# Revit family: Plumbing_Fixtures_Grohe_Rapido_T_Thermostatic_Concealed_Mixer_35500000_14_METRIC
name_source: partatom
category: Plumbing Fixtures
revit_build: Autodesk Revit 2014 (Build: 20130308_1515(x64)
units: mm (PartAtom-declared; Revit-internal decimal feet)

## types (1)
- Plumbing_Fixtures_Grohe_Rapido_T_Thermostatic_Concealed_Mixer_35500000_14_METRIC
    ADA Compliant = Yes
    Adjuster Head Width = 50 mm  [stored 0.164042 ft]
    Adjuster Stem Height = 20 mm  [stored 0.0656168 ft]
    Assembly Code = D2010
    AssetType = Fixed
    Button Height = 20 mm  [stored 0.0656168 ft]
    Button Width = 10 mm  [stored 0.0328084 ft]
    CW Connection = Yes
    CWFU = 4.5
    ClassificationName = Uniclass 2015
    ClassificationValue = Pr_40_20_87_98
    Cost = 0 $
    Default Elevation = 600 mm
    Depth = 86 mm
    Description = High flow rate up to 50 l/min by use of three outlets. Bottom outlet 1/2 can be used only with separate stop valve. Safe to install, stable built-in-box and protective cap. Fixation options for solid walls and dry cladding. Material for wall sealing included. Aquadimmer-diverter for bath mixer or stop valve for shower mixer in finishing trim set. Body in DR-brass. Built-in non return valves and dirt strainers
    Disc Length = 182 mm
    DocumentationInstallationGuide = http://cdn08.grohe.com
    DocumentationLiterature = http://cdn08.grohe.com
    DocumentationMaintenance = http://cdn08.grohe.com
    DocumentationTechnical = http://cdn08.grohe.com
    DurationUnit = Years
    Ecojoy = Yes
    ExpectedLife = 0
    Faucet Material = Grohe-Chrome
    Features = GROHE EcoJoy. GROHE TurboStat. Universal thermostatic mixer for concealed installation
    HW Connection = Yes
    HWFU = 4.5
    Handle Width = 15 mm  [stored 0.0492126 ft]
    Keynote = N13
    Length = 139 mm
    Low Emitting Material = Yes
    Manufacturer = Grohe Limited
    Mixed Water Radius = 5 mm  [stored 0.0164042 ft]
    Model = Rapido T Universal thermostatic mixer
    NBSDescription = Water supply fittings for wash basins and troughs
    NBSObjectName = Water supply fittings for wash basins and troughs
    NBSReference = 45-35-70/371
    Name = Rapido T Universal thermostatic mixer
    Percentage of Recycled Content = 0
    Product Page URL = http://www.grohe.com
    ProductionYear = 2016
    Spare Parts List = http://www.grohe.com
    Top Bolt Height = 20 mm  [stored 0.0656168 ft]
    Type Comments = Rapido T thermostatic Universal mixer - 35500000
    TypeName = Rapido T thermostatic Universal mixer - 35500000
    URL = www.grohe.com
    Vent Connection = No
    WFU = 0
    WarrantyDurationUnit = Years
    Waste Connection = No
    Width = 174 mm
    _BIMspec_GUID = 0
    _current revision = 1
    _distributed by = www.bimstore.co.uk

note: [stored X ft] marks values corroborated as IEEE doubles in the binary element streams (Revit-internal decimal feet)

## geometry (parser evidence)
native form markers: Blend x6, Sweep x1
no freeform markers — native parametric forms only
